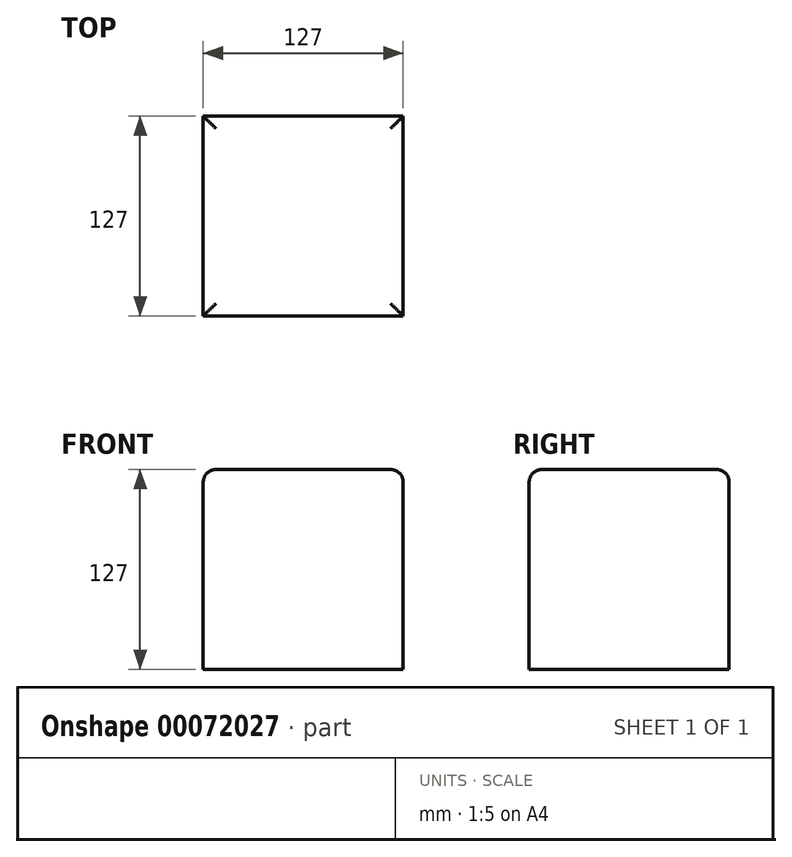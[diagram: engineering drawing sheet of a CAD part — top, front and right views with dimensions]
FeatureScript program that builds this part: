
annotation { "Feature Type Name" : "Feature", "Feature Type Description" : "" }
export const myFeature = defineFeature(function(context is Context, id is Id, definition is map)
    precondition{}
    {
        {
            var Q0;
            Q0=qCreatedBy(makeId("Front.planeOp"),FACE);
            var sketch = newSketch(context, id + "F0", { "sketchPlane" : qUnion([Q0])});
            skLineSegment(sketch, "E0.rect.bottom", {"start": v(63.5, -63.5) * mm, "end": v(-63.5, -63.5) * mm});
            skLineSegment(sketch, "E0.rect.top", {"start": v(63.5, 63.5) * mm, "end": v(-63.5, 63.5) * mm});
            skLineSegment(sketch, "E0.rect.left", {"start": v(63.5, -63.5) * mm, "end": v(63.5, 63.5) * mm});
            skLineSegment(sketch, "E0.rect.right", {"start": v(-63.5, -63.5) * mm, "end": v(-63.5, 63.5) * mm});
            skPoint(sketch, "E0.rect.middle", {"position": v(0, 0) * mm});
            skSolve(sketch);
        }
        {
            var Q0;
            Q0 = qSketchRegion(id + "F0", true);
            extrude(context, id + "F1", {"entities" : qUnion([Q0]), "endBound" : BoundingType.SYMMETRIC, "depth" : 127 * mm});
        }
        {
            var Q0;
            Q0=makeQuery(id+"F1.opExtrude","SWEPT_FACE",FACE,{"disambiguationData":[OSD([sQuery(id+"F0.wireOp",EDGE,"E0.rect.top")])]});
            fillet(context, id + "F2", {"entities" : qUnion([Q0]), "radius" : 8 * mm, "tangentPropagation" : true, "allowEdgeOverflow" : false});
        }
        {
            var Q0;
            Q0=makeQuery(id+"F1.opExtrude","SWEPT_FACE",FACE,{"disambiguationData":[OSD([sQuery(id+"F0.wireOp",EDGE,"E0.rect.top")])]});
            var sketch = newSketch(context, id + "F3", { "sketchPlane" : qUnion([Q0])});
            skCircle(sketch, "E1", {"center": v(0, 0) * mm, "radius": 46.3 * mm});
            skSolve(sketch);
        }
        {
            var Q0;
            Q0=sQuery(id+"F3.wireOp",EDGE,"E1");
            extrude(context, id + "F4", {"bodyType" : ToolBodyType.SURFACE, "surfaceEntities" : qUnion([Q0]), "depth" : 100 * mm, "hasSecondDirection" : true, "secondDirectionOppositeDirection" : true, "secondDirectionDepth" : 200 * mm});
        }
    });
